# Revit family: IS_TonicII_R4310_BIM_GB
name_source: partatom
category: Plumbing Fixtures
revit_build: Autodesk Revit MEP 2014 (Build: 20140709_2115(x64)
units: mm (PartAtom-declared; Revit-internal decimal feet)

## types (15) — shared parameters
Accessories = www.idealspec.co.uk
AreaUnits = millimeters
Assembly Code = C1030200
AssetType = Fixed
BREEAM = No
Brand = Ideal Standard
Category = Furniture
CodePerformance = EN 14749:2005
ConnectionType = Plumbing
Default Elevation = 800 mm  [stored 2.62467 ft]
DurationUnit = year
ECA = No
ExpectedLife = 30
HandleMatl = ISI_IdealStandard_Handle_Silver_Render
IfcExportAs = IfcFurnitureType
IfcExportType = USERDEFINED
InstallationInstructions = www.idealspec.co.uk/resources.html
LinearUnits = millimeters
Manufacturer = Ideal Standard (UK) Ltd
ManufacturerURL = www.idealspec.co.uk
NBSDescription = Bathroom integrated duct work
NBSReference = 45-35-72/320
NominalDepth = 440 mm  [stored 1.44357 ft]
NominalHeight = 120 mm  [stored 0.393701 ft]
NominalLength = 440 mm  [stored 1.44357 ft]
Shape = Rectangular
Space = Internal
SpareParts = www.fastpart-spares.co.uk
TMV3 = No
URL = www.idealspec.co.uk
Uniclass2015Description = Bathroom integrated duct work
Uniclass2015Reference = Pr_40_30_78_04
Uniclass2015Version = Products v1.1
Version = 1
VolumeUnits = Litres
WRAS = No
WarrantyDescription = Manufacturers Warranty
WarrantyDurationParts = 5
WarrantyDurationUnit = year
WaterEfficientProduct = No
zero-valued in all types: CWFU, Cost, HWFU

## per-type parameters (varying)
| type | BIMObjectName | BarCode | Color | Description | Features | Finish | LaminateFinish | Model | ModelNumber | ModelReference | Name | NettWeight | NominalWidth | ProductInformation | Size |
| R4310FE - Tonic II 600mm Shelf Unit - Wood Light Grey | ISI_IdealStandard_Furniture_TonicII_R4310FE | 3391500572096 | Light Grey Wood | Tonic II 600mm shelf unit | 600mm shelf unit | Light Grey Wood | ISI_IdealStandard_Sanitaryware_WoodLightGreyFE_Render | R4310FE | R4310FE | Tonic II 600mm shelf unit | ISI_Furniture_TonicII_R4310FE_IdealStandard | 4.5 Kg | 597 mm | www.idealspec.co.uk/datasheets/R4310FE | 120 x 440 x 597 mm |
| R4310FF - Tonic II 600mm Shelf Unit - Wood Light Brown | ISI_IdealStandard_Furniture_TonicII_R4310FF | 3391500572089 | Light Brown Wood | Tonic II 600mm shelf unit | 600mm shelf unit | Light Brown Wood | ISI_IdealStandard_Sanitaryware_WoodLightBrownFF_Render | R4310FF | R4310FF | Tonic II 600mm shelf unit | ISI_Furniture_TonicII_R4310FF_IdealStandard | 4.5 Kg | 597 mm | www.idealspec.co.uk/datasheets/R4310FF | 120 x 440 x 597 mm |
| R4310FC - Tonic II 600mm Shelf Unit - Gloss Light Brown | ISI_IdealStandard_Furniture_TonicII_R4310FC | 3391500572072 | Light Brown Gloss | Tonic II 600mm shelf unit | 600mm shelf unit | Light Brown Gloss | ISI_IdealStandard_Sanitaryware_GlossLightBrownFC_Render | R4310FC | R4310FC | Tonic II 600mm shelf unit | ISI_Furniture_TonicII_R4310FC_IdealStandard | 4.5 Kg | 597 mm | www.idealspec.co.uk/datasheets/R4310FC | 120 x 440 x 597 mm |
| R4310FA - Tonic II 600mm Shelf Unit - Gloss light Grey | ISI_IdealStandard_Furniture_TonicII_R4310FA | 3391500572065 | Light Grey Gloss | Tonic II 600mm shelf unit | 600mm shelf unit | Light Grey Gloss | ISI_IdealStandard_Sanitaryware_GlossLightGreyFA_Render | R4310FA | R4310FA | Tonic II 600mm shelf unit | ISI_Furniture_TonicII_R4310FA_IdealStandard | 4.5 Kg | 597 mm | www.idealspec.co.uk/datasheets/R4310FA | 120 x 440 x 597 mm |
| R4310WG - Tonic II 600mm Shelf Unit - White Gloss | ISI_IdealStandard_Furniture_TonicII_R4310WG | 3391500572058 | Gloss White | Tonic II 600mm shelf unit | 600mm shelf unit | Gloss White | ISI_IdealStandard_Sanitaryware_WhiteGlossWG_Render | R4310WG | R4310WG | Tonic II 600mm shelf unit | ISI_Furniture_TonicII_R4310WG_IdealStandard | 4.5 Kg | 597 mm | www.idealspec.co.uk/datasheets/R4310WG | 120 x 440 x 597 mm |
| R4311WG - Tonic II 800mm Shelf Unit - White Gloss | ISI_IdealStandard_Furniture_TonicII_R4311WG | 3391500572102 | Gloss White | Tonic II 800mm shelf unit | 800mm shelf unit | Gloss White | ISI_IdealStandard_Sanitaryware_WhiteGlossWG_Render | R4311WG | R4311WG | Tonic II 800mm shelf unit | ISI_Furniture_TonicII_R4311WG_IdealStandard | 5 Kg | 797 mm  [stored 2.61483 ft] | www.idealspec.co.uk/datasheets/R4311WG | 120 x 440 x 797 mm |
| R4311FF - Tonic II 800mm Shelf Unit - Wood Light Brown | ISI_IdealStandard_Furniture_TonicII_R4311FF | 3391500572133 | Light Brown Wood | Tonic II 800mm shelf unit | 800mm shelf unit | Light Brown Wood | ISI_IdealStandard_Sanitaryware_WoodLightBrownFF_Render | R4311FF | R4311FF | Tonic II 800mm shelf unit | ISI_Furniture_TonicII_R4311FF_IdealStandard | 5 Kg | 797 mm  [stored 2.61483 ft] | www.idealspec.co.uk/datasheets/R4311FF | 120 x 440 x 797 mm |
| R4311FE - Tonic II 800mm Shelf Unit - Wood Light Grey | ISI_IdealStandard_Furniture_TonicII_R4311FE | 3391500572140 | Light Grey Wood | Tonic II 800mm shelf unit | 800mm shelf unit | Light Grey Wood | ISI_IdealStandard_Sanitaryware_WoodLightGreyFE_Render | R4311FE | R4311FE | Tonic II 800mm shelf unit | ISI_Furniture_TonicII_R4311FE_IdealStandard | 5 Kg | 797 mm  [stored 2.61483 ft] | www.idealspec.co.uk/datasheets/R4311FE | 120 x 440 x 797 mm |
| R4311FA - Tonic II 800mm Shelf Unit - Gloss Light Grey | ISI_IdealStandard_Furniture_TonicII_R4311FA | 3391500572119 | Light Grey Gloss | Tonic II 800mm shelf unit | 800mm shelf unit | Light Grey Gloss | ISI_IdealStandard_Sanitaryware_GlossLightGreyFA_Render | R4311FA | R4311FA | Tonic II 800mm shelf unit | ISI_Furniture_TonicII_R4311FA_IdealStandard | 5 Kg | 797 mm  [stored 2.61483 ft] | www.idealspec.co.uk/datasheets/R4311FA | 120 x 440 x 797 mm |
| R4311FC - Tonic II 800mm Shelf Unit - Gloss Light Brown | ISI_IdealStandard_Furniture_TonicII_R4311FC | 3391500572126 | Light Brown Gloss | Tonic II 800mm shelf unit | 800mm shelf unit | Light Brown Gloss | ISI_IdealStandard_Sanitaryware_GlossLightBrownFC_Render | R4311FC | R4311FC | Tonic II 800mm shelf unit | ISI_Furniture_TonicII_R4311FC_IdealStandard | 5 Kg | 797 mm  [stored 2.61483 ft] | www.idealspec.co.uk/datasheets/R4311FC | 120 x 440 x 797 mm |
| R4312FE - Tonic II 1000mm Shelf Unit - Wood Light Grey | ISI_IdealStandard_Furniture_TonicII_R4312FE | 3391500572195 | Light Grey Wood | Tonic II 1000mm shelf unit | 1000mm shelf unit | Light Grey Wood | ISI_IdealStandard_Sanitaryware_WoodLightGreyFE_Render | R4312FE | R4312FE | Tonic II 1000mm shelf unit | ISI_Furniture_TonicII_R4312FE_IdealStandard | 5.5 Kg | 997 mm | www.idealspec.co.uk/datasheets/R4312FE | 120 x 440 x 997 mm |
| R4312FF - Tonic II 1000mm Shelf Unit - Wood Light Brown | ISI_IdealStandard_Furniture_TonicII_R4312FF | 3391500572188 | Light Brown Wood | Tonic II 1000mm shelf unit | 1000mm shelf unit | Light Brown Wood | ISI_IdealStandard_Sanitaryware_WoodLightBrownFF_Render | R4312FF | R4312FF | Tonic II 1000mm shelf unit | ISI_Furniture_TonicII_R4312FF_IdealStandard | 5.5 Kg | 997 mm | www.idealspec.co.uk/datasheets/R4312FF | 120 x 440 x 997 mm |
| R4312FA - Tonic II 1000mm Shelf Unit - Gloss Light Grey | ISI_IdealStandard_Furniture_TonicII_R4312FA | 3391500572164 | Light Grey Gloss | Tonic II 1000mm shelf unit | 1000mm shelf unit | Light Grey Gloss | ISI_IdealStandard_Sanitaryware_GlossLightGreyFA_Render | R4312FA | R4312FA | Tonic II 1000mm shelf unit | ISI_Furniture_TonicII_R4312FA_IdealStandard | 5.5 Kg | 997 mm | www.idealspec.co.uk/datasheets/R4312FA | 120 x 440 x 997 mm |
| R4312FC - Tonic II 1000mm Shelf Unit - Gloss Light Brown | ISI_IdealStandard_Furniture_TonicII_R4312FC | 3391500572171 | Light Brown Gloss | Tonic II 1000mm shelf unit | 1000mm shelf unit | Light Brown Gloss | ISI_IdealStandard_Sanitaryware_GlossLightBrownFC_Render | R4312FC | R4312FC | Tonic II 1000mm shelf unit | ISI_Furniture_TonicII_R4312FC_IdealStandard | 5.5 Kg | 997 mm | www.idealspec.co.uk/datasheets/R4312FC | 120 x 440 x 997 mm |
| R4312WG - Tonic II 1000mm Shelf Unit - White Gloss | ISI_IdealStandard_Furniture_TonicII_R4312WG | 3391500572157 | Gloss White | Tonic II 1000mm shelf unit | 1000mm shelf unit | Gloss White | ISI_IdealStandard_Sanitaryware_WhiteGlossWG_Render | R4312WG | R4312WG | Tonic II 1000mm shelf unit | ISI_Furniture_TonicII_R4312WG_IdealStandard | 5.5 Kg | 997 mm | www.idealspec.co.uk/datasheets/R4312WG | 120 x 440 x 997 mm |

note: [stored X ft] marks values corroborated as IEEE doubles in the binary element streams (Revit-internal decimal feet)

## geometry (parser evidence)
native form markers: Sweep x3
no freeform markers — native parametric forms only
